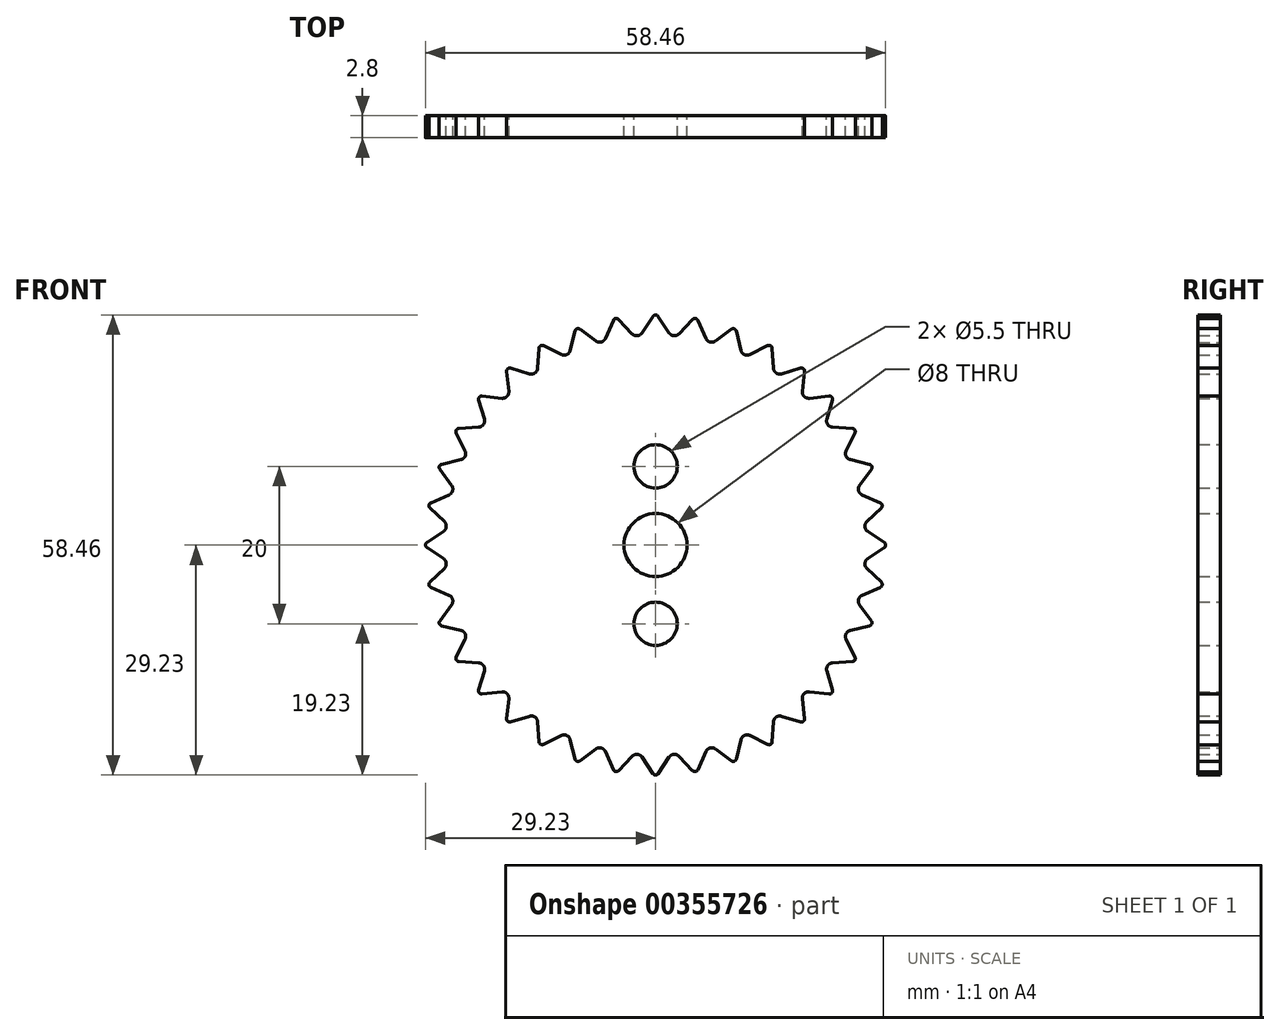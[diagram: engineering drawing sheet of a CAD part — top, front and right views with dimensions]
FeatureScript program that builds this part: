
annotation { "Feature Type Name" : "Feature", "Feature Type Description" : "" }
export const myFeature = defineFeature(function(context is Context, id is Id, definition is map)
    precondition{}
    {
        {
            var Q0;
            Q0=qCreatedBy(makeId("Front.planeOp"),FACE);
            var sketch = newSketch(context, id + "F0", { "sketchPlane" : qUnion([Q0])});
            skCircle(sketch, "E0", {"center": v(0, 0) * mm, "radius": 4 * mm});
            skCircle(sketch, "E1", {"center": v(0, -10) * mm, "radius": 2.75 * mm});
            skCircle(sketch, "E2.MirrorC", {"center": v(0, 10) * mm, "radius": 2.75 * mm});
            skLineSegment(sketch, "E3", {"start": v(-1.73, 26.95) * mm, "end": v(-0.33, 29.05) * mm});
            skLineSegment(sketch, "E4", {"start": v(0.33, 29.05) * mm, "end": v(1.73, 26.95) * mm});
            skPoint(sketch, "E5.visualSharp", {"position": v(0, 29.55) * mm});
            skCircle(sketch, "E6", {"center": v(0, 0) * mm, "radius": 14 * mm});
            skArc(sketch, "E7.filletArc", {"start": v(0.33, 29.05) * mm, "mid": v(0, 29.23) * mm, "end": v(-0.33, 29.05) * mm});
            skLineSegment(sketch, "E8.1.0", {"start": v(-6.38, 26.24) * mm, "end": v(-5.37, 28.55) * mm});
            skArc(sketch, "E8.1.1", {"start": v(-4.72, 28.66) * mm, "mid": v(-5.08, 28.78) * mm, "end": v(-5.37, 28.55) * mm});
            skLineSegment(sketch, "E8.1.2", {"start": v(-4.72, 28.66) * mm, "end": v(-2.98, 26.84) * mm});
            skLineSegment(sketch, "E8.2.0", {"start": v(-10.84, 24.73) * mm, "end": v(-10.25, 27.18) * mm});
            skArc(sketch, "E8.2.1", {"start": v(-9.62, 27.41) * mm, "mid": v(-10, 27.46) * mm, "end": v(-10.25, 27.18) * mm});
            skLineSegment(sketch, "E8.2.2", {"start": v(-9.62, 27.41) * mm, "end": v(-7.6, 25.91) * mm});
            skLineSegment(sketch, "E8.3.0", {"start": v(-14.97, 22.47) * mm, "end": v(-14.81, 24.99) * mm});
            skArc(sketch, "E8.3.1", {"start": v(-14.24, 25.32) * mm, "mid": v(-14.61, 25.31) * mm, "end": v(-14.81, 24.99) * mm});
            skLineSegment(sketch, "E8.3.2", {"start": v(-14.24, 25.32) * mm, "end": v(-11.97, 24.2) * mm});
            skLineSegment(sketch, "E8.4.0", {"start": v(-18.65, 19.53) * mm, "end": v(-18.93, 22.04) * mm});
            skArc(sketch, "E8.4.1", {"start": v(-18.42, 22.47) * mm, "mid": v(-18.79, 22.39) * mm, "end": v(-18.93, 22.04) * mm});
            skLineSegment(sketch, "E8.4.2", {"start": v(-18.42, 22.47) * mm, "end": v(-16, 21.75) * mm});
            skLineSegment(sketch, "E8.5.0", {"start": v(-21.75, 16) * mm, "end": v(-22.47, 18.42) * mm});
            skArc(sketch, "E8.5.1", {"start": v(-22.04, 18.93) * mm, "mid": v(-22.39, 18.79) * mm, "end": v(-22.47, 18.42) * mm});
            skLineSegment(sketch, "E8.5.2", {"start": v(-22.04, 18.93) * mm, "end": v(-19.53, 18.65) * mm});
            skLineSegment(sketch, "E8.6.0", {"start": v(-24.2, 11.97) * mm, "end": v(-25.32, 14.24) * mm});
            skArc(sketch, "E8.6.1", {"start": v(-24.99, 14.81) * mm, "mid": v(-25.31, 14.61) * mm, "end": v(-25.32, 14.24) * mm});
            skLineSegment(sketch, "E8.6.2", {"start": v(-24.99, 14.81) * mm, "end": v(-22.47, 14.97) * mm});
            skLineSegment(sketch, "E8.7.0", {"start": v(-25.91, 7.6) * mm, "end": v(-27.41, 9.62) * mm});
            skArc(sketch, "E8.7.1", {"start": v(-27.18, 10.25) * mm, "mid": v(-27.46, 10) * mm, "end": v(-27.41, 9.62) * mm});
            skLineSegment(sketch, "E8.7.2", {"start": v(-27.18, 10.25) * mm, "end": v(-24.73, 10.84) * mm});
            skLineSegment(sketch, "E8.8.0", {"start": v(-26.84, 2.98) * mm, "end": v(-28.66, 4.72) * mm});
            skArc(sketch, "E8.8.1", {"start": v(-28.55, 5.37) * mm, "mid": v(-28.78, 5.08) * mm, "end": v(-28.66, 4.72) * mm});
            skLineSegment(sketch, "E8.8.2", {"start": v(-28.55, 5.37) * mm, "end": v(-26.24, 6.38) * mm});
            skLineSegment(sketch, "E8.9.0", {"start": v(-26.95, -1.73) * mm, "end": v(-29.05, -0.33) * mm});
            skArc(sketch, "E8.9.1", {"start": v(-29.05, 0.33) * mm, "mid": v(-29.23, 0) * mm, "end": v(-29.05, -0.33) * mm});
            skLineSegment(sketch, "E8.9.2", {"start": v(-29.05, 0.33) * mm, "end": v(-26.95, 1.73) * mm});
            skLineSegment(sketch, "E8.10.0", {"start": v(-26.24, -6.38) * mm, "end": v(-28.55, -5.37) * mm});
            skArc(sketch, "E8.10.1", {"start": v(-28.66, -4.72) * mm, "mid": v(-28.78, -5.08) * mm, "end": v(-28.55, -5.37) * mm});
            skLineSegment(sketch, "E8.10.2", {"start": v(-28.66, -4.72) * mm, "end": v(-26.84, -2.98) * mm});
            skLineSegment(sketch, "E8.11.0", {"start": v(-24.73, -10.84) * mm, "end": v(-27.18, -10.25) * mm});
            skArc(sketch, "E8.11.1", {"start": v(-27.41, -9.62) * mm, "mid": v(-27.46, -10) * mm, "end": v(-27.18, -10.25) * mm});
            skLineSegment(sketch, "E8.11.2", {"start": v(-27.41, -9.62) * mm, "end": v(-25.91, -7.6) * mm});
            skLineSegment(sketch, "E8.12.0", {"start": v(-22.47, -14.97) * mm, "end": v(-24.99, -14.81) * mm});
            skArc(sketch, "E8.12.1", {"start": v(-25.32, -14.24) * mm, "mid": v(-25.31, -14.61) * mm, "end": v(-24.99, -14.81) * mm});
            skLineSegment(sketch, "E8.12.2", {"start": v(-25.32, -14.24) * mm, "end": v(-24.2, -11.97) * mm});
            skLineSegment(sketch, "E8.13.0", {"start": v(-19.53, -18.65) * mm, "end": v(-22.04, -18.93) * mm});
            skArc(sketch, "E8.13.1", {"start": v(-22.47, -18.42) * mm, "mid": v(-22.39, -18.79) * mm, "end": v(-22.04, -18.93) * mm});
            skLineSegment(sketch, "E8.13.2", {"start": v(-22.47, -18.42) * mm, "end": v(-21.75, -16) * mm});
            skLineSegment(sketch, "E8.14.0", {"start": v(-16, -21.75) * mm, "end": v(-18.42, -22.47) * mm});
            skArc(sketch, "E8.14.1", {"start": v(-18.93, -22.04) * mm, "mid": v(-18.79, -22.39) * mm, "end": v(-18.42, -22.47) * mm});
            skLineSegment(sketch, "E8.14.2", {"start": v(-18.93, -22.04) * mm, "end": v(-18.65, -19.53) * mm});
            skLineSegment(sketch, "E8.15.0", {"start": v(-11.97, -24.2) * mm, "end": v(-14.24, -25.32) * mm});
            skArc(sketch, "E8.15.1", {"start": v(-14.81, -24.99) * mm, "mid": v(-14.61, -25.31) * mm, "end": v(-14.24, -25.32) * mm});
            skLineSegment(sketch, "E8.15.2", {"start": v(-14.81, -24.99) * mm, "end": v(-14.97, -22.47) * mm});
            skLineSegment(sketch, "E8.16.0", {"start": v(-7.39, -25.76) * mm, "end": v(-9.62, -27.41) * mm});
            skArc(sketch, "E8.16.1", {"start": v(-10.25, -27.18) * mm, "mid": v(-10, -27.46) * mm, "end": v(-9.62, -27.41) * mm});
            skLineSegment(sketch, "E8.16.2", {"start": v(-10.25, -27.18) * mm, "end": v(-10.84, -24.73) * mm});
            skLineSegment(sketch, "E8.17.0", {"start": v(-2.98, -26.84) * mm, "end": v(-4.72, -28.66) * mm});
            skArc(sketch, "E8.17.1", {"start": v(-5.37, -28.55) * mm, "mid": v(-5.08, -28.78) * mm, "end": v(-4.72, -28.66) * mm});
            skLineSegment(sketch, "E8.17.2", {"start": v(-5.37, -28.55) * mm, "end": v(-6.38, -26.24) * mm});
            skLineSegment(sketch, "E8.18.0", {"start": v(1.73, -26.95) * mm, "end": v(0.33, -29.05) * mm});
            skArc(sketch, "E8.18.1", {"start": v(-0.33, -29.05) * mm, "mid": v(0, -29.23) * mm, "end": v(0.33, -29.05) * mm});
            skLineSegment(sketch, "E8.18.2", {"start": v(-0.33, -29.05) * mm, "end": v(-1.73, -26.95) * mm});
            skLineSegment(sketch, "E8.19.0", {"start": v(6.38, -26.24) * mm, "end": v(5.37, -28.55) * mm});
            skArc(sketch, "E8.19.1", {"start": v(4.72, -28.66) * mm, "mid": v(5.08, -28.78) * mm, "end": v(5.37, -28.55) * mm});
            skLineSegment(sketch, "E8.19.2", {"start": v(4.72, -28.66) * mm, "end": v(2.98, -26.84) * mm});
            skLineSegment(sketch, "E8.20.0", {"start": v(10.84, -24.73) * mm, "end": v(10.25, -27.18) * mm});
            skArc(sketch, "E8.20.1", {"start": v(9.62, -27.41) * mm, "mid": v(10, -27.46) * mm, "end": v(10.25, -27.18) * mm});
            skLineSegment(sketch, "E8.20.2", {"start": v(9.62, -27.41) * mm, "end": v(7.6, -25.91) * mm});
            skLineSegment(sketch, "E8.21.0", {"start": v(14.97, -22.47) * mm, "end": v(14.81, -24.99) * mm});
            skArc(sketch, "E8.21.1", {"start": v(14.24, -25.32) * mm, "mid": v(14.61, -25.31) * mm, "end": v(14.81, -24.99) * mm});
            skLineSegment(sketch, "E8.21.2", {"start": v(14.24, -25.32) * mm, "end": v(11.97, -24.2) * mm});
            skLineSegment(sketch, "E8.22.0", {"start": v(18.65, -19.53) * mm, "end": v(18.93, -22.04) * mm});
            skArc(sketch, "E8.22.1", {"start": v(18.42, -22.47) * mm, "mid": v(18.79, -22.39) * mm, "end": v(18.93, -22.04) * mm});
            skLineSegment(sketch, "E8.22.2", {"start": v(18.42, -22.47) * mm, "end": v(16, -21.75) * mm});
            skLineSegment(sketch, "E8.23.0", {"start": v(21.75, -16) * mm, "end": v(22.47, -18.42) * mm});
            skArc(sketch, "E8.23.1", {"start": v(22.04, -18.93) * mm, "mid": v(22.39, -18.79) * mm, "end": v(22.47, -18.42) * mm});
            skLineSegment(sketch, "E8.23.2", {"start": v(22.04, -18.93) * mm, "end": v(19.53, -18.65) * mm});
            skLineSegment(sketch, "E8.24.0", {"start": v(24.2, -11.97) * mm, "end": v(25.32, -14.24) * mm});
            skArc(sketch, "E8.24.1", {"start": v(24.99, -14.81) * mm, "mid": v(25.31, -14.61) * mm, "end": v(25.32, -14.24) * mm});
            skLineSegment(sketch, "E8.24.2", {"start": v(24.99, -14.81) * mm, "end": v(22.47, -14.97) * mm});
            skLineSegment(sketch, "E8.25.0", {"start": v(25.91, -7.6) * mm, "end": v(27.41, -9.62) * mm});
            skArc(sketch, "E8.25.1", {"start": v(27.18, -10.25) * mm, "mid": v(27.46, -10) * mm, "end": v(27.41, -9.62) * mm});
            skLineSegment(sketch, "E8.25.2", {"start": v(27.18, -10.25) * mm, "end": v(24.73, -10.84) * mm});
            skLineSegment(sketch, "E8.26.0", {"start": v(26.84, -2.98) * mm, "end": v(28.66, -4.72) * mm});
            skArc(sketch, "E8.26.1", {"start": v(28.55, -5.37) * mm, "mid": v(28.78, -5.08) * mm, "end": v(28.66, -4.72) * mm});
            skLineSegment(sketch, "E8.26.2", {"start": v(28.55, -5.37) * mm, "end": v(26.24, -6.38) * mm});
            skLineSegment(sketch, "E8.27.0", {"start": v(26.95, 1.73) * mm, "end": v(29.05, 0.33) * mm});
            skArc(sketch, "E8.27.1", {"start": v(29.05, -0.33) * mm, "mid": v(29.23, 0) * mm, "end": v(29.05, 0.33) * mm});
            skLineSegment(sketch, "E8.27.2", {"start": v(29.05, -0.33) * mm, "end": v(26.95, -1.73) * mm});
            skLineSegment(sketch, "E8.28.0", {"start": v(26.24, 6.38) * mm, "end": v(28.55, 5.37) * mm});
            skArc(sketch, "E8.28.1", {"start": v(28.66, 4.72) * mm, "mid": v(28.78, 5.08) * mm, "end": v(28.55, 5.37) * mm});
            skLineSegment(sketch, "E8.28.2", {"start": v(28.66, 4.72) * mm, "end": v(26.84, 2.98) * mm});
            skLineSegment(sketch, "E8.29.0", {"start": v(24.73, 10.84) * mm, "end": v(27.18, 10.25) * mm});
            skArc(sketch, "E8.29.1", {"start": v(27.41, 9.62) * mm, "mid": v(27.46, 10) * mm, "end": v(27.18, 10.25) * mm});
            skLineSegment(sketch, "E8.29.2", {"start": v(27.41, 9.62) * mm, "end": v(25.91, 7.6) * mm});
            skLineSegment(sketch, "E8.30.0", {"start": v(22.47, 14.97) * mm, "end": v(24.99, 14.81) * mm});
            skArc(sketch, "E8.30.1", {"start": v(25.32, 14.24) * mm, "mid": v(25.31, 14.61) * mm, "end": v(24.99, 14.81) * mm});
            skLineSegment(sketch, "E8.30.2", {"start": v(25.32, 14.24) * mm, "end": v(24.2, 11.97) * mm});
            skLineSegment(sketch, "E8.31.0", {"start": v(19.53, 18.65) * mm, "end": v(22.04, 18.93) * mm});
            skArc(sketch, "E8.31.1", {"start": v(22.47, 18.42) * mm, "mid": v(22.39, 18.79) * mm, "end": v(22.04, 18.93) * mm});
            skLineSegment(sketch, "E8.31.2", {"start": v(22.47, 18.42) * mm, "end": v(21.75, 16) * mm});
            skLineSegment(sketch, "E8.32.0", {"start": v(16, 21.75) * mm, "end": v(18.42, 22.47) * mm});
            skArc(sketch, "E8.32.1", {"start": v(18.93, 22.04) * mm, "mid": v(18.79, 22.39) * mm, "end": v(18.42, 22.47) * mm});
            skLineSegment(sketch, "E8.32.2", {"start": v(18.93, 22.04) * mm, "end": v(18.65, 19.53) * mm});
            skLineSegment(sketch, "E8.33.0", {"start": v(11.97, 24.2) * mm, "end": v(14.24, 25.32) * mm});
            skArc(sketch, "E8.33.1", {"start": v(14.81, 24.99) * mm, "mid": v(14.61, 25.31) * mm, "end": v(14.24, 25.32) * mm});
            skLineSegment(sketch, "E8.33.2", {"start": v(14.81, 24.99) * mm, "end": v(14.97, 22.47) * mm});
            skLineSegment(sketch, "E8.34.0", {"start": v(7.6, 25.91) * mm, "end": v(9.62, 27.41) * mm});
            skArc(sketch, "E8.34.1", {"start": v(10.25, 27.18) * mm, "mid": v(10, 27.46) * mm, "end": v(9.62, 27.41) * mm});
            skLineSegment(sketch, "E8.34.2", {"start": v(10.25, 27.18) * mm, "end": v(10.84, 24.73) * mm});
            skLineSegment(sketch, "E8.35.0", {"start": v(2.98, 26.84) * mm, "end": v(4.72, 28.66) * mm});
            skArc(sketch, "E8.35.1", {"start": v(5.37, 28.55) * mm, "mid": v(5.08, 28.78) * mm, "end": v(4.72, 28.66) * mm});
            skLineSegment(sketch, "E8.35.2", {"start": v(5.37, 28.55) * mm, "end": v(6.38, 26.24) * mm});
            skPoint(sketch, "E9.newPointA", {"position": v(1.87, 26.73) * mm});
            skPoint(sketch, "E9.newPointB", {"position": v(2.8, 26.65) * mm});
            skArc(sketch, "E9.filletArc", {"start": v(1.73, 26.95) * mm, "mid": v(2.33, 26.6) * mm, "end": v(2.98, 26.84) * mm});
            skArc(sketch, "E10.1.0", {"start": v(-2.98, 26.84) * mm, "mid": v(-2.33, 26.6) * mm, "end": v(-1.73, 26.95) * mm});
            skArc(sketch, "E10.2.0", {"start": v(-7.6, 25.91) * mm, "mid": v(-6.9, 25.78) * mm, "end": v(-6.38, 26.24) * mm});
            skArc(sketch, "E10.3.0", {"start": v(-11.97, 24.2) * mm, "mid": v(-11.28, 24.2) * mm, "end": v(-10.84, 24.73) * mm});
            skArc(sketch, "E10.4.0", {"start": v(-16, 21.75) * mm, "mid": v(-15.31, 21.87) * mm, "end": v(-14.97, 22.47) * mm});
            skArc(sketch, "E10.5.0", {"start": v(-19.53, 18.65) * mm, "mid": v(-18.87, 18.87) * mm, "end": v(-18.65, 19.53) * mm});
            skArc(sketch, "E10.6.0", {"start": v(-22.47, 14.97) * mm, "mid": v(-21.87, 15.31) * mm, "end": v(-21.75, 16) * mm});
            skArc(sketch, "E10.7.0", {"start": v(-24.73, 10.84) * mm, "mid": v(-24.2, 11.28) * mm, "end": v(-24.2, 11.97) * mm});
            skArc(sketch, "E10.8.0", {"start": v(-26.24, 6.38) * mm, "mid": v(-25.78, 6.9) * mm, "end": v(-25.91, 7.6) * mm});
            skArc(sketch, "E10.9.0", {"start": v(-26.95, 1.73) * mm, "mid": v(-26.6, 2.33) * mm, "end": v(-26.84, 2.98) * mm});
            skArc(sketch, "E10.10.0", {"start": v(-26.84, -2.98) * mm, "mid": v(-26.6, -2.33) * mm, "end": v(-26.95, -1.73) * mm});
            skArc(sketch, "E10.11.0", {"start": v(-25.91, -7.6) * mm, "mid": v(-25.78, -6.9) * mm, "end": v(-26.24, -6.38) * mm});
            skArc(sketch, "E10.12.0", {"start": v(-24.2, -11.97) * mm, "mid": v(-24.2, -11.28) * mm, "end": v(-24.73, -10.84) * mm});
            skArc(sketch, "E10.13.0", {"start": v(-21.75, -16) * mm, "mid": v(-21.87, -15.31) * mm, "end": v(-22.47, -14.97) * mm});
            skArc(sketch, "E10.14.0", {"start": v(-18.65, -19.53) * mm, "mid": v(-18.87, -18.87) * mm, "end": v(-19.53, -18.65) * mm});
            skArc(sketch, "E10.15.0", {"start": v(-14.97, -22.47) * mm, "mid": v(-15.31, -21.87) * mm, "end": v(-16, -21.75) * mm});
            skArc(sketch, "E10.16.0", {"start": v(-10.84, -24.73) * mm, "mid": v(-11.28, -24.2) * mm, "end": v(-11.97, -24.2) * mm});
            skArc(sketch, "E10.17.0", {"start": v(-6.38, -26.24) * mm, "mid": v(-6.9, -25.78) * mm, "end": v(-7.6, -25.91) * mm});
            skArc(sketch, "E10.18.0", {"start": v(-1.73, -26.95) * mm, "mid": v(-2.33, -26.6) * mm, "end": v(-2.98, -26.84) * mm});
            skArc(sketch, "E10.19.0", {"start": v(2.98, -26.84) * mm, "mid": v(2.33, -26.6) * mm, "end": v(1.73, -26.95) * mm});
            skArc(sketch, "E10.20.0", {"start": v(7.6, -25.91) * mm, "mid": v(6.9, -25.78) * mm, "end": v(6.38, -26.24) * mm});
            skArc(sketch, "E10.21.0", {"start": v(11.97, -24.2) * mm, "mid": v(11.28, -24.2) * mm, "end": v(10.84, -24.73) * mm});
            skArc(sketch, "E10.22.0", {"start": v(16, -21.75) * mm, "mid": v(15.31, -21.87) * mm, "end": v(14.97, -22.47) * mm});
            skArc(sketch, "E10.23.0", {"start": v(19.53, -18.65) * mm, "mid": v(18.87, -18.87) * mm, "end": v(18.65, -19.53) * mm});
            skArc(sketch, "E10.24.0", {"start": v(22.47, -14.97) * mm, "mid": v(21.87, -15.31) * mm, "end": v(21.75, -16) * mm});
            skArc(sketch, "E10.25.0", {"start": v(24.73, -10.84) * mm, "mid": v(24.2, -11.28) * mm, "end": v(24.2, -11.97) * mm});
            skArc(sketch, "E10.26.0", {"start": v(26.24, -6.38) * mm, "mid": v(25.78, -6.9) * mm, "end": v(25.91, -7.6) * mm});
            skArc(sketch, "E10.27.0", {"start": v(26.95, -1.73) * mm, "mid": v(26.6, -2.33) * mm, "end": v(26.84, -2.98) * mm});
            skArc(sketch, "E10.28.0", {"start": v(26.84, 2.98) * mm, "mid": v(26.6, 2.33) * mm, "end": v(26.95, 1.73) * mm});
            skArc(sketch, "E10.29.0", {"start": v(25.91, 7.6) * mm, "mid": v(25.78, 6.9) * mm, "end": v(26.24, 6.38) * mm});
            skArc(sketch, "E10.30.0", {"start": v(24.2, 11.97) * mm, "mid": v(24.2, 11.28) * mm, "end": v(24.73, 10.84) * mm});
            skArc(sketch, "E10.31.0", {"start": v(21.75, 16) * mm, "mid": v(21.87, 15.31) * mm, "end": v(22.47, 14.97) * mm});
            skArc(sketch, "E10.32.0", {"start": v(18.65, 19.53) * mm, "mid": v(18.87, 18.87) * mm, "end": v(19.53, 18.65) * mm});
            skArc(sketch, "E10.33.0", {"start": v(14.97, 22.47) * mm, "mid": v(15.31, 21.87) * mm, "end": v(16, 21.75) * mm});
            skArc(sketch, "E10.34.0", {"start": v(10.84, 24.73) * mm, "mid": v(11.28, 24.2) * mm, "end": v(11.97, 24.2) * mm});
            skArc(sketch, "E10.35.0", {"start": v(6.38, 26.24) * mm, "mid": v(6.9, 25.78) * mm, "end": v(7.6, 25.91) * mm});
            skPoint(sketch, "E11.orphan", {"position": v(11.75, 24.09) * mm});
            skPoint(sketch, "E12.orphan", {"position": v(14.99, 22.22) * mm});
            skPoint(sketch, "E13.orphan", {"position": v(15.75, 21.68) * mm});
            skPoint(sketch, "E14.orphan", {"position": v(18.62, 19.28) * mm});
            skPoint(sketch, "E15.orphan", {"position": v(19.28, 18.62) * mm});
            skPoint(sketch, "E16.orphan", {"position": v(21.68, 15.75) * mm});
            skPoint(sketch, "E17.orphan", {"position": v(22.22, 14.99) * mm});
            skPoint(sketch, "E18.orphan", {"position": v(24.09, 11.75) * mm});
            skPoint(sketch, "E19.orphan", {"position": v(24.48, 10.9) * mm});
            skPoint(sketch, "E20.orphan", {"position": v(25.76, 7.39) * mm});
            skPoint(sketch, "E21.orphan", {"position": v(26, 6.48) * mm});
            skPoint(sketch, "E22.orphan", {"position": v(26.65, 2.8) * mm});
            skPoint(sketch, "E23.orphan", {"position": v(26.73, 1.87) * mm});
            skPoint(sketch, "E24.orphan", {"position": v(26.73, -1.87) * mm});
            skPoint(sketch, "E25.orphan", {"position": v(26.65, -2.8) * mm});
            skPoint(sketch, "E26.orphan", {"position": v(26, -6.48) * mm});
            skPoint(sketch, "E27.orphan", {"position": v(25.76, -7.39) * mm});
            skPoint(sketch, "E28.orphan", {"position": v(24.48, -10.9) * mm});
            skPoint(sketch, "E29.orphan", {"position": v(24.09, -11.75) * mm});
            skPoint(sketch, "E30.orphan", {"position": v(22.22, -14.99) * mm});
            skPoint(sketch, "E31.orphan", {"position": v(21.68, -15.75) * mm});
            skPoint(sketch, "E32.orphan", {"position": v(19.28, -18.62) * mm});
            skPoint(sketch, "E33.orphan", {"position": v(18.62, -19.28) * mm});
            skPoint(sketch, "E34.orphan", {"position": v(15.75, -21.68) * mm});
            skPoint(sketch, "E35.orphan", {"position": v(14.99, -22.22) * mm});
            skPoint(sketch, "E36.orphan", {"position": v(11.75, -24.09) * mm});
            skPoint(sketch, "E37.orphan", {"position": v(10.9, -24.48) * mm});
            skPoint(sketch, "E38.orphan", {"position": v(7.39, -25.76) * mm});
            skPoint(sketch, "E39.orphan", {"position": v(6.48, -26) * mm});
            skPoint(sketch, "E40.orphan", {"position": v(2.8, -26.65) * mm});
            skPoint(sketch, "E41.orphan", {"position": v(1.87, -26.73) * mm});
            skPoint(sketch, "E42.orphan", {"position": v(-1.87, -26.73) * mm});
            skPoint(sketch, "E43.orphan", {"position": v(-2.8, -26.65) * mm});
            skPoint(sketch, "E44.orphan", {"position": v(-6.48, -26) * mm});
            skPoint(sketch, "E45.orphan", {"position": v(-10.9, -24.48) * mm});
            skPoint(sketch, "E46.orphan", {"position": v(-11.75, -24.09) * mm});
            skPoint(sketch, "E47.orphan", {"position": v(-14.99, -22.22) * mm});
            skPoint(sketch, "E48.orphan", {"position": v(-15.75, -21.68) * mm});
            skPoint(sketch, "E49.orphan", {"position": v(-18.62, -19.28) * mm});
            skPoint(sketch, "E50.orphan", {"position": v(-19.28, -18.62) * mm});
            skPoint(sketch, "E51.orphan", {"position": v(-21.68, -15.75) * mm});
            skPoint(sketch, "E52.orphan", {"position": v(-22.22, -14.99) * mm});
            skPoint(sketch, "E53.orphan", {"position": v(-24.09, -11.75) * mm});
            skPoint(sketch, "E54.orphan", {"position": v(-24.48, -10.9) * mm});
            skPoint(sketch, "E55.orphan", {"position": v(-25.76, -7.39) * mm});
            skPoint(sketch, "E56.orphan", {"position": v(-26, -6.48) * mm});
            skPoint(sketch, "E57.orphan", {"position": v(-26.65, -2.8) * mm});
            skPoint(sketch, "E58.orphan", {"position": v(-26.73, -1.87) * mm});
            skPoint(sketch, "E59.orphan", {"position": v(-26.73, 1.87) * mm});
            skPoint(sketch, "E60.orphan", {"position": v(-26.65, 2.8) * mm});
            skPoint(sketch, "E61.orphan", {"position": v(-26, 6.48) * mm});
            skPoint(sketch, "E62.orphan", {"position": v(-25.76, 7.39) * mm});
            skPoint(sketch, "E63.orphan", {"position": v(-24.48, 10.9) * mm});
            skPoint(sketch, "E64.orphan", {"position": v(-24.09, 11.75) * mm});
            skPoint(sketch, "E65.orphan", {"position": v(-22.22, 14.99) * mm});
            skPoint(sketch, "E66.orphan", {"position": v(-21.68, 15.75) * mm});
            skPoint(sketch, "E67.orphan", {"position": v(-19.28, 18.62) * mm});
            skPoint(sketch, "E68.orphan", {"position": v(-18.62, 19.28) * mm});
            skPoint(sketch, "E69.orphan", {"position": v(-15.75, 21.68) * mm});
            skPoint(sketch, "E70.orphan", {"position": v(-14.99, 22.22) * mm});
            skPoint(sketch, "E71.orphan", {"position": v(-11.75, 24.09) * mm});
            skPoint(sketch, "E72.orphan", {"position": v(-10.9, 24.48) * mm});
            skPoint(sketch, "E73.orphan", {"position": v(-7.39, 25.76) * mm});
            skPoint(sketch, "E74.orphan", {"position": v(-6.48, 26) * mm});
            skPoint(sketch, "E75.orphan", {"position": v(-2.8, 26.65) * mm});
            skPoint(sketch, "E76.orphan", {"position": v(-1.87, 26.73) * mm});
            skPoint(sketch, "E77.orphan", {"position": v(10.9, 24.48) * mm});
            skPoint(sketch, "E78.orphan", {"position": v(6.48, 26) * mm});
            skPoint(sketch, "E79.orphan", {"position": v(7.39, 25.76) * mm});
            skSolve(sketch);
        }
        {
            var Q0;
            Q0=makeQuery(id+"F0.imprint","IMPRINT",FACE,{"disambiguationData":[TD([[makeQuery(id+"F0.imprint","IMPRINT",EDGE,{"derivedFrom":sQuery(id+"F0.wireOp",EDGE,"E0")}),-1.0]])]});
            var Q1;
            Q1=makeQuery(id+"F0.imprint","IMPRINT",FACE,{"disambiguationData":[TD([[makeQuery(id+"F0.imprint","IMPRINT",EDGE,{"derivedFrom":sQuery(id+"F0.wireOp",EDGE,"E3")}),-1.0]])]});
            extrude(context, id + "F1", {"entities" : qUnion([Q0, Q1]), "depth" : 2.8 * mm});
        }
    });
